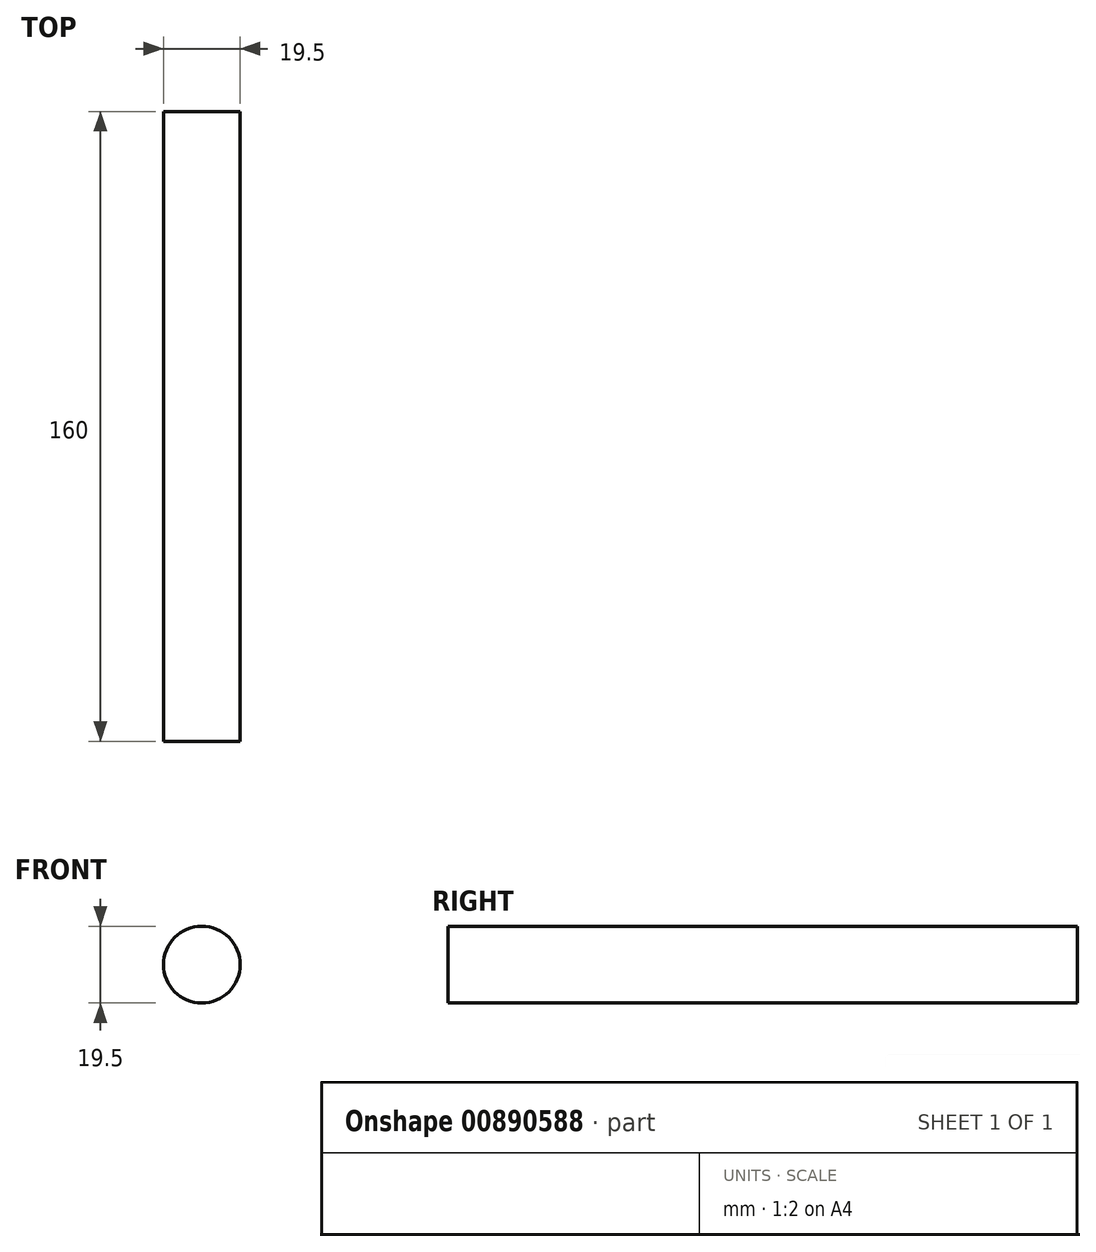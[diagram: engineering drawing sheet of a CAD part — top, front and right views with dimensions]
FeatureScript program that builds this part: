
annotation { "Feature Type Name" : "Feature", "Feature Type Description" : "" }
export const myFeature = defineFeature(function(context is Context, id is Id, definition is map)
    precondition{}
    {
        {
            var Q0;
            Q0=qCreatedBy(makeId("Front.planeOp"),FACE);
            var sketch = newSketch(context, id + "F0", { "sketchPlane" : qUnion([Q0])});
            skCircle(sketch, "E0", {"center": v(0, 0) * mm, "radius": 9.75 * mm});
            skSolve(sketch);
        }
        {
            var Q0;
            Q0 = qSketchRegion(id + "F0", true);
            extrude(context, id + "F1", {"entities" : qUnion([Q0]), "depth" : 160 * mm, "offsetDistance" : 25 * mm});
        }
    });
